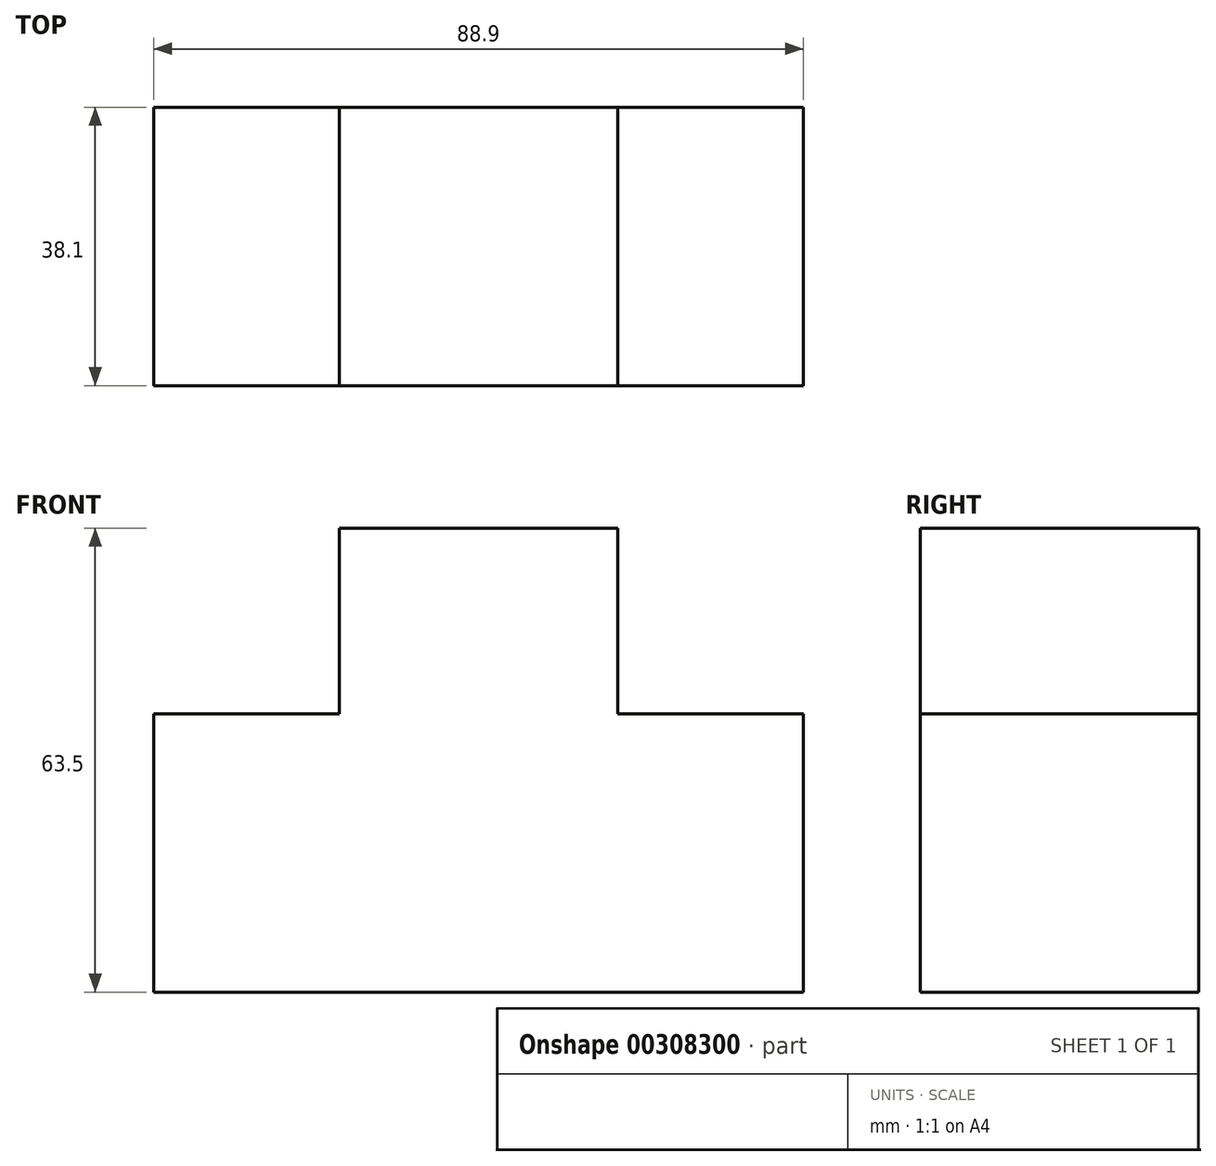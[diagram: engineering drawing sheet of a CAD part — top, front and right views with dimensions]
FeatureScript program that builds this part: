
annotation { "Feature Type Name" : "Feature", "Feature Type Description" : "" }
export const myFeature = defineFeature(function(context is Context, id is Id, definition is map)
    precondition{}
    {
        {
            var Q0;
            Q0=qCreatedBy(makeId("Front.planeOp"),FACE);
            var sketch = newSketch(context, id + "F0", { "sketchPlane" : qUnion([Q0])});
            skLineSegment(sketch, "E0", {"start": v(-42.89, -34.61) * mm, "end": v(46.01, -34.61) * mm});
            skLineSegment(sketch, "E1", {"start": v(-42.89, -34.61) * mm, "end": v(-42.89, 3.49) * mm});
            skLineSegment(sketch, "E2", {"start": v(-42.89, 3.49) * mm, "end": v(-17.49, 3.49) * mm});
            skLineSegment(sketch, "E3", {"start": v(-17.49, 3.49) * mm, "end": v(-17.49, 28.89) * mm});
            skLineSegment(sketch, "E4", {"start": v(-17.49, 28.89) * mm, "end": v(20.61, 28.89) * mm});
            skLineSegment(sketch, "E5", {"start": v(20.61, 28.89) * mm, "end": v(20.61, 3.49) * mm});
            skLineSegment(sketch, "E6", {"start": v(20.61, 3.49) * mm, "end": v(46.01, 3.49) * mm});
            skLineSegment(sketch, "E7", {"start": v(46.01, 3.49) * mm, "end": v(46.01, -34.61) * mm});
            skSolve(sketch);
        }
        {
            var Q0;
            Q0=makeQuery(id+"F0.imprint","IMPRINT",FACE,{"disambiguationData":[TD([[makeQuery(id+"F0.imprint","IMPRINT",EDGE,{"derivedFrom":sQuery(id+"F0.wireOp",EDGE,"E0")}),1.0]])]});
            extrude(context, id + "F1", {"entities" : qUnion([Q0]), "depth" : 38.1 * mm});
        }
    });
